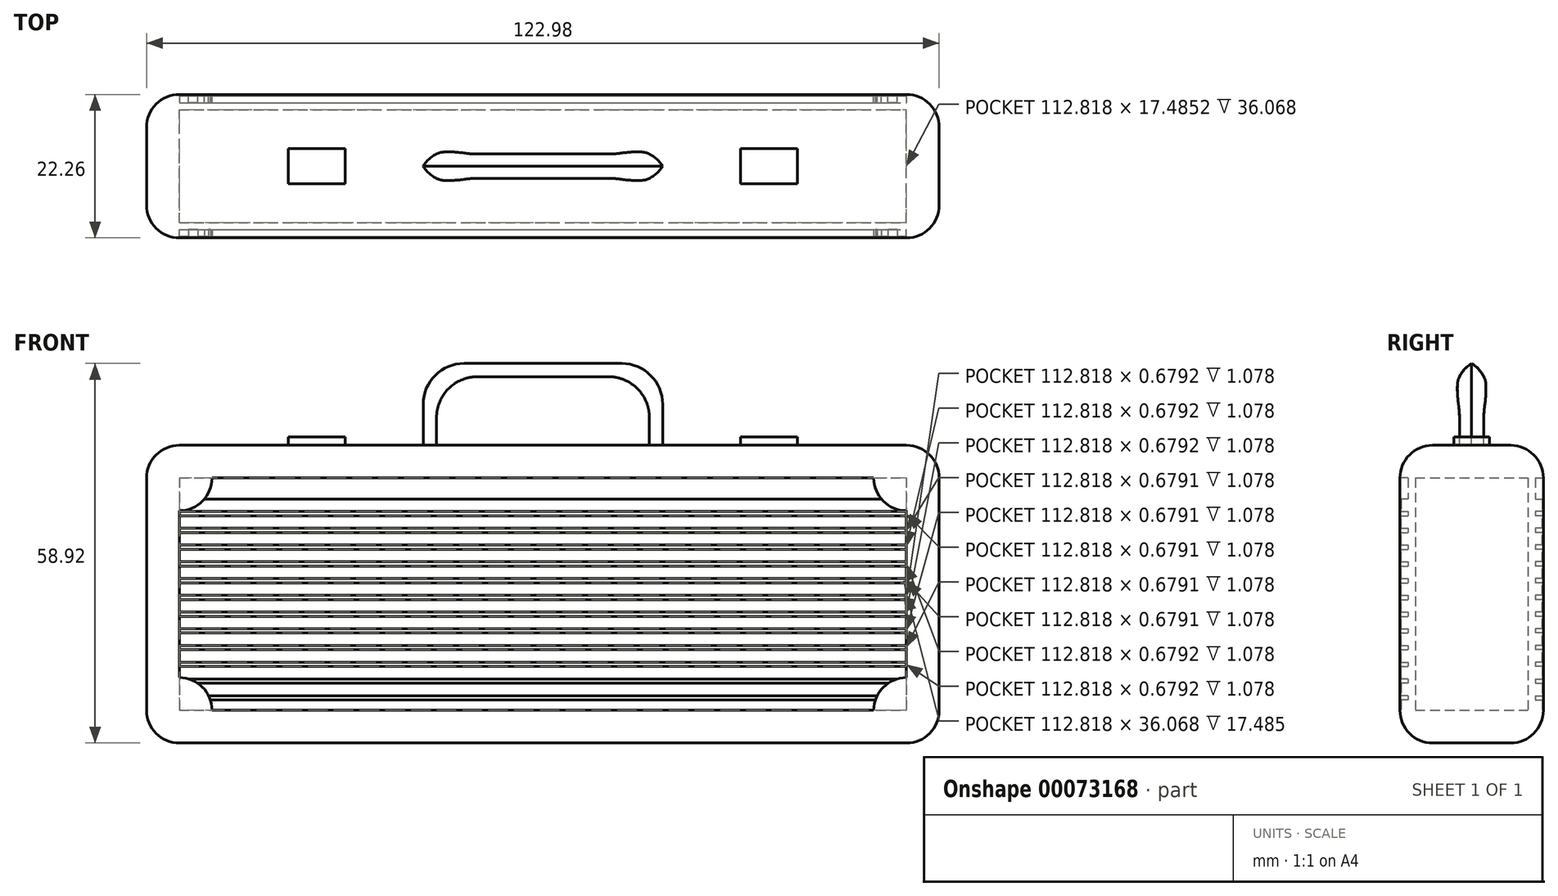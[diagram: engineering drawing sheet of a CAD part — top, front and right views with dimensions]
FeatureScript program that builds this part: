
annotation { "Feature Type Name" : "Feature", "Feature Type Description" : "" }
export const myFeature = defineFeature(function(context is Context, id is Id, definition is map)
    precondition{}
    {
        {
            var Q0;
            Q0=qCreatedBy(makeId("Front.planeOp"),FACE);
            var sketch = newSketch(context, id + "F0", { "sketchPlane" : qUnion([Q0])});
            skLineSegment(sketch, "E0.bottom", {"start": v(61.49, -23.11) * mm, "end": v(-61.49, -23.11) * mm});
            skLineSegment(sketch, "E0.top", {"start": v(61.49, 23.11) * mm, "end": v(-61.49, 23.11) * mm});
            skLineSegment(sketch, "E0.left", {"start": v(61.49, -23.11) * mm, "end": v(61.49, 23.11) * mm});
            skLineSegment(sketch, "E0.right", {"start": v(-61.49, -23.11) * mm, "end": v(-61.49, 23.11) * mm});
            skPoint(sketch, "E0.middle", {"position": v(0, 0) * mm});
            skSolve(sketch);
        }
        {
            var Q0;
            Q0=makeQuery(id+"F0.imprint","IMPRINT",FACE,{"disambiguationData":[TD([[makeQuery(id+"F0.imprint","IMPRINT",EDGE,{"derivedFrom":sQuery(id+"F0.wireOp",EDGE,"E0.bottom")}),-1.0]])]});
            extrude(context, id + "F1", {"entities" : qUnion([Q0]), "depth" : 11.13 * mm});
        }
        {
            var Q0;
            Q0=makeQuery(id+"F1.opExtrude","SWEPT_EDGE",EDGE,{"disambiguationData":[OSD([sQuery(id+"F0.wireOp",EDGE,"E0.top"),sQuery(id+"F0.wireOp",EDGE,"E0.right")])]});
            var Q1;
            Q1=makeQuery(id+"F1.opExtrude","CAP_EDGE",EDGE,{"disambiguationData":[OSD([sQuery(id+"F0.wireOp",EDGE,"E0.right")])],"isStart":false});
            var Q2;
            Q2=makeQuery(id+"F1.opExtrude","CAP_EDGE",EDGE,{"disambiguationData":[OSD([sQuery(id+"F0.wireOp",EDGE,"E0.top")])],"isStart":false});
            var Q3;
            Q3=makeQuery(id+"F1.opExtrude","SWEPT_EDGE",EDGE,{"disambiguationData":[OSD([sQuery(id+"F0.wireOp",EDGE,"E0.bottom"),sQuery(id+"F0.wireOp",EDGE,"E0.right")])]});
            var Q4;
            Q4=makeQuery(id+"F1.opExtrude","CAP_EDGE",EDGE,{"disambiguationData":[OSD([sQuery(id+"F0.wireOp",EDGE,"E0.bottom")])],"isStart":false});
            var Q5;
            Q5=makeQuery(id+"F1.opExtrude","CAP_EDGE",EDGE,{"disambiguationData":[OSD([sQuery(id+"F0.wireOp",EDGE,"E0.left")])],"isStart":false});
            var Q6;
            Q6=makeQuery(id+"F1.opExtrude","SWEPT_EDGE",EDGE,{"disambiguationData":[OSD([sQuery(id+"F0.wireOp",EDGE,"E0.top"),sQuery(id+"F0.wireOp",EDGE,"E0.left")])]});
            var Q7;
            Q7=makeQuery(id+"F1.opExtrude","SWEPT_EDGE",EDGE,{"disambiguationData":[OSD([sQuery(id+"F0.wireOp",EDGE,"E0.bottom"),sQuery(id+"F0.wireOp",EDGE,"E0.left")])]});
            fillet(context, id + "F2", {"entities" : qUnion([Q0, Q1, Q2, Q3, Q4, Q5, Q6, Q7]), "radius" : 5.08 * mm, "tangentPropagation" : true, "allowEdgeOverflow" : false});
        }
        {
            var Q0;
            Q0=qCreatedBy(makeId("Front.planeOp"),FACE);
            var sketch = newSketch(context, id + "F3", { "sketchPlane" : qUnion([Q0])});
            skPoint(sketch, "E1.0", {"position": v(-56.4, 18.03) * mm});
            skPoint(sketch, "E2.0", {"position": v(56.4, -18.03) * mm});
            skLineSegment(sketch, "E3.bottom", {"start": v(-56.4, 18.03) * mm, "end": v(56.4, 18.03) * mm});
            skLineSegment(sketch, "E3.top", {"start": v(-56.4, -18.03) * mm, "end": v(56.4, -18.03) * mm});
            skLineSegment(sketch, "E3.left", {"start": v(-56.4, 18.03) * mm, "end": v(-56.4, -18.03) * mm});
            skLineSegment(sketch, "E3.right", {"start": v(56.4, 18.03) * mm, "end": v(56.4, -18.03) * mm});
            skSolve(sketch);
        }
        {
            var Q0;
            Q0 = qSketchRegion(id + "F3", true);
            extrude(context, id + "F4", {"entities" : qUnion([Q0]), "operationType" : NewBodyOperationType.REMOVE, "depth" : 8.74 * mm});
        }
        {
            var Q0;
            Q0=makeQuery(id+"F1.opExtrude","CAP_FACE",FACE,{"disambiguationData":[OSD([sQuery(id+"F0.wireOp",EDGE,"E0.bottom"),sQuery(id+"F0.wireOp",EDGE,"E0.top"),sQuery(id+"F0.wireOp",EDGE,"E0.left"),sQuery(id+"F0.wireOp",EDGE,"E0.right")])],"isStart":false});
            cPlane(context, id + "F5", {"entities" : qUnion([Q0]), "cplaneType" : CPlaneType.OFFSET, "offset" : 0 * mm, "width" : 152.4 * mm, "height" : 152.4 * mm});
        }
        {
            var Q0;
            Q0=qCreatedBy(id+"F5.planeOp",FACE);
            var sketch = newSketch(context, id + "F6", { "sketchPlane" : qUnion([Q0])});
            skPoint(sketch, "E4.0", {"position": v(-56.4, 18.03) * mm});
            skPoint(sketch, "E5.0", {"position": v(56.4, -18.03) * mm});
            skLineSegment(sketch, "E6.bottom", {"start": v(-56.4, 18.03) * mm, "end": v(56.4, 18.03) * mm});
            skLineSegment(sketch, "E6.top", {"start": v(-56.4, -18.03) * mm, "end": v(56.4, -18.03) * mm});
            skLineSegment(sketch, "E6.left", {"start": v(-56.4, 18.03) * mm, "end": v(-56.4, -18.03) * mm});
            skLineSegment(sketch, "E6.right", {"start": v(56.4, 18.03) * mm, "end": v(56.4, -18.03) * mm});
            skSolve(sketch);
        }
        {
            var Q0;
            Q0 = qSketchRegion(id + "F6", true);
            extrude(context, id + "F7", {"entities" : qUnion([Q0]), "operationType" : NewBodyOperationType.REMOVE, "oppositeDirection" : true, "depth" : 1.27 * mm});
        }
        {
            var Q0;
            Q0=qCreatedBy(id+"F5.planeOp",FACE);
            var sketch = newSketch(context, id + "F8", { "sketchPlane" : qUnion([Q0])});
            skLineSegment(sketch, "E7.0", {"start": v(-56.4, 18.03) * mm, "end": v(-56.4, -18.03) * mm});
            skLineSegment(sketch, "E8.0", {"start": v(56.4, 18.03) * mm, "end": v(-56.4, 18.03) * mm});
            skLineSegment(sketch, "E9", {"start": v(-56.4, 18.03) * mm, "end": v(-50.64, 18.03) * mm});
            skLineSegment(sketch, "E10", {"start": v(-56.4, 18.03) * mm, "end": v(-56.4, 14.08) * mm});
            skSolve(sketch);
        }
        {
            var Q0;
            Q0=makeQuery(id+"F1.opExtrude","SWEPT_FACE",FACE,{"disambiguationData":[OSD([sQuery(id+"F0.wireOp",EDGE,"E0.top")])]});
            cPlane(context, id + "F9", {"entities" : qUnion([Q0]), "cplaneType" : CPlaneType.OFFSET, "offset" : 0 * mm, "width" : 152.4 * mm, "height" : 152.4 * mm});
        }
        {
            var Q0;
            Q0=makeQuery(id+"F1.opExtrude","CAP_FACE",FACE,{"disambiguationData":[OSD([sQuery(id+"F0.wireOp",EDGE,"E0.bottom"),sQuery(id+"F0.wireOp",EDGE,"E0.top"),sQuery(id+"F0.wireOp",EDGE,"E0.left"),sQuery(id+"F0.wireOp",EDGE,"E0.right")])],"isStart":true});
            cPlane(context, id + "F10", {"entities" : qUnion([Q0]), "cplaneType" : CPlaneType.OFFSET, "offset" : 0 * mm, "width" : 152.4 * mm, "height" : 152.4 * mm});
        }
        {
            var Q0;
            Q0=qCreatedBy(id+"F10.planeOp",FACE);
            var sketch = newSketch(context, id + "F11", { "sketchPlane" : qUnion([Q0])});
            skLineSegment(sketch, "E11.0", {"start": v(-56.4, 23.11) * mm, "end": v(56.4, 23.11) * mm});
            skLineSegment(sketch, "E12.bottom", {"start": v(-18.58, 23.11) * mm, "end": v(18.58, 23.11) * mm});
            skLineSegment(sketch, "E12.top", {"start": v(-12.23, 35.81) * mm, "end": v(12.23, 35.81) * mm});
            skLineSegment(sketch, "E12.left", {"start": v(-18.58, 23.11) * mm, "end": v(-18.58, 29.46) * mm});
            skLineSegment(sketch, "E12.right", {"start": v(18.58, 23.11) * mm, "end": v(18.58, 29.46) * mm});
            skPoint(sketch, "E12.middle", {"position": v(0, 29.46) * mm});
            skPoint(sketch, "E13.visualSharp", {"position": v(18.58, 35.81) * mm});
            skArc(sketch, "E13.filletArc", {"start": v(18.58, 29.46) * mm, "mid": v(16.72, 33.95) * mm, "end": v(12.23, 35.81) * mm});
            skPoint(sketch, "E14.visualSharp", {"position": v(-18.58, 35.81) * mm});
            skArc(sketch, "E14.filletArc", {"start": v(-12.23, 35.81) * mm, "mid": v(-16.72, 33.95) * mm, "end": v(-18.58, 29.46) * mm});
            skLineSegment(sketch, "E15.top", {"start": v(-10.17, 33.76) * mm, "end": v(10.15, 33.76) * mm});
            skLineSegment(sketch, "E15.left", {"start": v(-16.52, 23.11) * mm, "end": v(-16.52, 27.41) * mm});
            skLineSegment(sketch, "E15.right", {"start": v(16.5, 23.11) * mm, "end": v(16.5, 27.41) * mm});
            skArc(sketch, "E16.filletArc", {"start": v(16.5, 27.41) * mm, "mid": v(14.64, 31.9) * mm, "end": v(10.15, 33.76) * mm});
            skArc(sketch, "E17.filletArc", {"start": v(-10.17, 33.76) * mm, "mid": v(-14.66, 31.9) * mm, "end": v(-16.52, 27.41) * mm});
            skSolve(sketch);
        }
        {
            var Q0;
            Q0=makeQuery(id+"F11.imprint","IMPRINT",FACE,{"disambiguationData":[TD([[makeQuery(id+"F11.imprint","IMPRINT",EDGE,{"derivedFrom":sQuery(id+"F11.wireOp",EDGE,"E12.top")}),-1.0]])]});
            extrude(context, id + "F12", {"entities" : qUnion([Q0]), "operationType" : NewBodyOperationType.ADD, "oppositeDirection" : true, "depth" : 2.42 * mm});
        }
        {
            var Q0;
            Q0=makeQuery(id+"F12.opExtrude","CAP_EDGE",EDGE,{"disambiguationData":[OSD([sQuery(id+"F11.wireOp",EDGE,"E13.filletArc")])],"isStart":false});
            fillet(context, id + "F13", {"entities" : qUnion([Q0]), "radius" : 5.08 * mm, "tangentPropagation" : true, "allowEdgeOverflow" : false});
        }
        {
            var Q0;
            Q0=makeQuery(id+"F7.boolean.opBoolean","COPY",FACE,{"derivedFrom":makeQuery(id+"F7.opExtrude","CAP_FACE",FACE,{"disambiguationData":[OSD([sQuery(id+"F6.wireOp",EDGE,"E6.bottom"),sQuery(id+"F6.wireOp",EDGE,"E6.top"),sQuery(id+"F6.wireOp",EDGE,"E6.left"),sQuery(id+"F6.wireOp",EDGE,"E6.right")])],"isStart":false})});
            cPlane(context, id + "F14", {"entities" : qUnion([Q0]), "cplaneType" : CPlaneType.OFFSET, "offset" : 0 * mm, "width" : 152.4 * mm, "height" : 152.4 * mm});
        }
        {
            var Q0;
            Q0=qCreatedBy(id+"F14.planeOp",FACE);
            var sketch = newSketch(context, id + "F15", { "sketchPlane" : qUnion([Q0])});
            skLineSegment(sketch, "E18.0.0", {"start": v(56.4, 18.03) * mm, "end": v(-56.4, 18.03) * mm});
            skLineSegment(sketch, "E18.0.1", {"start": v(-56.4, 18.03) * mm, "end": v(-56.4, -18.03) * mm});
            skLineSegment(sketch, "E18.0.2", {"start": v(-56.4, -18.03) * mm, "end": v(56.4, -18.03) * mm});
            skLineSegment(sketch, "E18.0.3", {"start": v(56.4, -18.03) * mm, "end": v(56.4, 18.03) * mm});
            skLineSegment(sketch, "E19.bottom", {"start": v(-56.4, 18.03) * mm, "end": v(56.4, 18.03) * mm});
            skLineSegment(sketch, "E19.top", {"start": v(-56.4, 14.76) * mm, "end": v(56.4, 14.76) * mm});
            skLineSegment(sketch, "E19.left", {"start": v(-56.4, 18.03) * mm, "end": v(-56.4, 14.76) * mm});
            skLineSegment(sketch, "E19.right", {"start": v(56.4, 18.03) * mm, "end": v(56.4, 14.76) * mm});
            skLineSegment(sketch, "E20.1.0.0", {"start": v(-56.4, 15.43) * mm, "end": v(56.4, 15.43) * mm});
            skLineSegment(sketch, "E20.1.0.1", {"start": v(-56.4, 12.16) * mm, "end": v(56.4, 12.16) * mm});
            skLineSegment(sketch, "E20.1.0.2", {"start": v(56.4, 15.43) * mm, "end": v(-56.4, 15.43) * mm});
            skLineSegment(sketch, "E20.1.0.3", {"start": v(56.4, 15.43) * mm, "end": v(56.4, 12.16) * mm});
            skLineSegment(sketch, "E20.2.0.0", {"start": v(-56.4, 12.83) * mm, "end": v(56.4, 12.83) * mm});
            skLineSegment(sketch, "E20.2.0.1", {"start": v(-56.4, 9.56) * mm, "end": v(56.4, 9.56) * mm});
            skLineSegment(sketch, "E20.2.0.2", {"start": v(56.4, 12.83) * mm, "end": v(-56.4, 12.83) * mm});
            skLineSegment(sketch, "E20.2.0.3", {"start": v(56.4, 12.83) * mm, "end": v(56.4, 9.56) * mm});
            skLineSegment(sketch, "E20.3.0.0", {"start": v(-56.4, 10.24) * mm, "end": v(56.4, 10.24) * mm});
            skLineSegment(sketch, "E20.3.0.1", {"start": v(-56.4, 6.96) * mm, "end": v(56.4, 6.96) * mm});
            skLineSegment(sketch, "E20.3.0.2", {"start": v(56.4, 10.24) * mm, "end": v(-56.4, 10.24) * mm});
            skLineSegment(sketch, "E20.3.0.3", {"start": v(56.4, 10.24) * mm, "end": v(56.4, 6.96) * mm});
            skLineSegment(sketch, "E20.4.0.0", {"start": v(-56.4, 7.64) * mm, "end": v(56.4, 7.64) * mm});
            skLineSegment(sketch, "E20.4.0.1", {"start": v(-56.4, 4.36) * mm, "end": v(56.4, 4.36) * mm});
            skLineSegment(sketch, "E20.4.0.2", {"start": v(56.4, 7.64) * mm, "end": v(-56.4, 7.64) * mm});
            skLineSegment(sketch, "E20.4.0.3", {"start": v(56.4, 7.64) * mm, "end": v(56.4, 4.36) * mm});
            skLineSegment(sketch, "E20.5.0.0", {"start": v(-56.4, 5.04) * mm, "end": v(56.4, 5.04) * mm});
            skLineSegment(sketch, "E20.5.0.1", {"start": v(-56.4, 1.76) * mm, "end": v(56.4, 1.76) * mm});
            skLineSegment(sketch, "E20.5.0.2", {"start": v(56.4, 5.04) * mm, "end": v(-56.4, 5.04) * mm});
            skLineSegment(sketch, "E20.5.0.3", {"start": v(56.4, 5.04) * mm, "end": v(56.4, 1.76) * mm});
            skLineSegment(sketch, "E20.6.0.0", {"start": v(-56.4, 2.44) * mm, "end": v(56.4, 2.44) * mm});
            skLineSegment(sketch, "E20.6.0.1", {"start": v(-56.4, -0.84) * mm, "end": v(56.4, -0.84) * mm});
            skLineSegment(sketch, "E20.6.0.2", {"start": v(56.4, 2.44) * mm, "end": v(-56.4, 2.44) * mm});
            skLineSegment(sketch, "E20.6.0.3", {"start": v(56.4, 2.44) * mm, "end": v(56.4, -0.84) * mm});
            skLineSegment(sketch, "E20.7.0.0", {"start": v(-56.4, -0.16) * mm, "end": v(56.4, -0.16) * mm});
            skLineSegment(sketch, "E20.7.0.1", {"start": v(-56.4, -3.44) * mm, "end": v(56.4, -3.44) * mm});
            skLineSegment(sketch, "E20.7.0.2", {"start": v(56.4, -0.16) * mm, "end": v(-56.4, -0.16) * mm});
            skLineSegment(sketch, "E20.7.0.3", {"start": v(56.4, -0.16) * mm, "end": v(56.4, -3.44) * mm});
            skLineSegment(sketch, "E20.8.0.0", {"start": v(-56.4, -2.76) * mm, "end": v(56.4, -2.76) * mm});
            skLineSegment(sketch, "E20.8.0.1", {"start": v(-56.4, -6.04) * mm, "end": v(56.4, -6.04) * mm});
            skLineSegment(sketch, "E20.8.0.2", {"start": v(56.4, -2.76) * mm, "end": v(-56.4, -2.76) * mm});
            skLineSegment(sketch, "E20.8.0.3", {"start": v(56.4, -2.76) * mm, "end": v(56.4, -6.04) * mm});
            skLineSegment(sketch, "E20.9.0.0", {"start": v(-56.4, -5.36) * mm, "end": v(56.4, -5.36) * mm});
            skLineSegment(sketch, "E20.9.0.1", {"start": v(-56.4, -8.64) * mm, "end": v(56.4, -8.64) * mm});
            skLineSegment(sketch, "E20.9.0.2", {"start": v(56.4, -5.36) * mm, "end": v(-56.4, -5.36) * mm});
            skLineSegment(sketch, "E20.9.0.3", {"start": v(56.4, -5.36) * mm, "end": v(56.4, -8.64) * mm});
            skLineSegment(sketch, "E20.10.0.0", {"start": v(-56.4, -7.96) * mm, "end": v(56.4, -7.96) * mm});
            skLineSegment(sketch, "E20.10.0.1", {"start": v(-56.4, -11.24) * mm, "end": v(56.4, -11.24) * mm});
            skLineSegment(sketch, "E20.10.0.2", {"start": v(56.4, -7.96) * mm, "end": v(-56.4, -7.96) * mm});
            skLineSegment(sketch, "E20.10.0.3", {"start": v(56.4, -7.96) * mm, "end": v(56.4, -11.24) * mm});
            skLineSegment(sketch, "E20.11.0.0", {"start": v(-56.4, -10.56) * mm, "end": v(56.4, -10.56) * mm});
            skLineSegment(sketch, "E20.11.0.1", {"start": v(-56.4, -13.84) * mm, "end": v(56.4, -13.84) * mm});
            skLineSegment(sketch, "E20.11.0.2", {"start": v(56.4, -10.56) * mm, "end": v(-56.4, -10.56) * mm});
            skLineSegment(sketch, "E20.11.0.3", {"start": v(56.4, -10.56) * mm, "end": v(56.4, -13.84) * mm});
            skLineSegment(sketch, "E20.12.0.0", {"start": v(-56.4, -13.16) * mm, "end": v(56.4, -13.16) * mm});
            skLineSegment(sketch, "E20.12.0.1", {"start": v(-56.4, -16.44) * mm, "end": v(56.4, -16.44) * mm});
            skLineSegment(sketch, "E20.12.0.2", {"start": v(56.4, -13.16) * mm, "end": v(-56.4, -13.16) * mm});
            skLineSegment(sketch, "E20.12.0.3", {"start": v(56.4, -13.16) * mm, "end": v(56.4, -16.44) * mm});
            skLineSegment(sketch, "E20.13.0.0", {"start": v(-56.4, -15.76) * mm, "end": v(56.4, -15.76) * mm});
            skLineSegment(sketch, "E20.13.0.1", {"start": v(-56.4, -19.04) * mm, "end": v(56.4, -19.04) * mm});
            skLineSegment(sketch, "E20.13.0.2", {"start": v(56.4, -15.76) * mm, "end": v(-56.4, -15.76) * mm});
            skLineSegment(sketch, "E20.13.0.3", {"start": v(56.4, -15.76) * mm, "end": v(56.4, -19.04) * mm});
            skLineSegment(sketch, "E20.direction1", {"start": v(-56.4, 14.76) * mm, "end": v(-56.4, 12.16) * mm, "construction": true});
            skSolve(sketch);
        }
        {
            var Q0;
            Q0=qCreatedBy(id+"F9.planeOp",FACE);
            var sketch = newSketch(context, id + "F16", { "sketchPlane" : qUnion([Q0])});
            skLineSegment(sketch, "E21.0", {"start": v(56.4, 0) * mm, "end": v(18.58, 0) * mm});
            skLineSegment(sketch, "E22.0", {"start": v(-18.58, 0) * mm, "end": v(-56.4, 0) * mm});
            skLineSegment(sketch, "E23.bottom", {"start": v(30.69, 0) * mm, "end": v(39.5, 0) * mm});
            skLineSegment(sketch, "E23.top", {"start": v(30.69, -2.76) * mm, "end": v(39.5, -2.76) * mm});
            skLineSegment(sketch, "E23.left", {"start": v(30.69, 0) * mm, "end": v(30.69, -2.76) * mm});
            skLineSegment(sketch, "E23.right", {"start": v(39.5, 0) * mm, "end": v(39.5, -2.76) * mm});
            skLineSegment(sketch, "E24.MirrorCS", {"start": v(-30.69, 0) * mm, "end": v(-30.69, -2.76) * mm});
            skLineSegment(sketch, "E25.MirrorCS", {"start": v(-30.69, 0) * mm, "end": v(-39.5, 0) * mm});
            skLineSegment(sketch, "E26.MirrorCS", {"start": v(-39.5, 0) * mm, "end": v(-39.5, -2.76) * mm});
            skLineSegment(sketch, "E27.MirrorCS", {"start": v(-30.69, -2.76) * mm, "end": v(-39.5, -2.76) * mm});
            skSolve(sketch);
        }
        {
            var Q0;
            Q0 = qSketchRegion(id + "F16", true);
            extrude(context, id + "F17", {"entities" : qUnion([Q0]), "operationType" : NewBodyOperationType.ADD, "depth" : 1.27 * mm});
        }
        {
            var Q0;
            Q0=qCreatedBy(id+"F5.planeOp",FACE);
            var sketch = newSketch(context, id + "F18", { "sketchPlane" : qUnion([Q0])});
            skPoint(sketch, "E28.0", {"position": v(-56.4, 18.03) * mm});
            skLineSegment(sketch, "E29.0", {"start": v(-56.4, 18.03) * mm, "end": v(-50.64, 18.03) * mm});
            skLineSegment(sketch, "E30.0", {"start": v(-56.4, 18.03) * mm, "end": v(-56.4, 14.08) * mm});
            skLineSegment(sketch, "E31.0", {"start": v(-56.4, 13.38) * mm, "end": v(-56.4, 12.84) * mm});
            skLineSegment(sketch, "E31.1", {"start": v(-56.4, 10.78) * mm, "end": v(-56.4, 10.24) * mm});
            skLineSegment(sketch, "E31.2", {"start": v(-56.4, 2.99) * mm, "end": v(-56.4, 2.44) * mm});
            skLineSegment(sketch, "E31.3", {"start": v(-56.4, 8.18) * mm, "end": v(-56.4, 7.64) * mm});
            skLineSegment(sketch, "E31.4", {"start": v(-56.4, 5.58) * mm, "end": v(-56.4, 5.04) * mm});
            skLineSegment(sketch, "E31.5", {"start": v(-56.4, 12.84) * mm, "end": v(-56.4, 10.78) * mm});
            skLineSegment(sketch, "E31.6", {"start": v(-56.4, 10.24) * mm, "end": v(-56.4, 8.18) * mm});
            skLineSegment(sketch, "E31.7", {"start": v(-56.4, 7.64) * mm, "end": v(-56.4, 5.58) * mm});
            skLineSegment(sketch, "E31.8", {"start": v(-56.4, 5.04) * mm, "end": v(-56.4, 2.99) * mm});
            skArc(sketch, "E32", {"start": v(-51.33, 18.03) * mm, "mid": v(-52.82, 14.44) * mm, "end": v(-56.4, 12.95) * mm});
            skArc(sketch, "E33.MirrorCS", {"start": v(-51.33, -18.03) * mm, "mid": v(-52.82, -14.44) * mm, "end": v(-56.4, -12.95) * mm});
            skArc(sketch, "E34.MirrorCS", {"start": v(51.33, 18.03) * mm, "mid": v(52.82, 14.44) * mm, "end": v(56.4, 12.95) * mm});
            skArc(sketch, "E35.MirrorCS", {"start": v(51.33, -18.03) * mm, "mid": v(52.82, -14.44) * mm, "end": v(56.4, -12.95) * mm});
            skLineSegment(sketch, "E36", {"start": v(-51.33, 18.03) * mm, "end": v(-56.4, 18.03) * mm});
            skLineSegment(sketch, "E37", {"start": v(-56.4, 18.03) * mm, "end": v(-56.4, 12.95) * mm});
            skLineSegment(sketch, "E38", {"start": v(-56.4, -12.95) * mm, "end": v(-56.4, -18.03) * mm});
            skLineSegment(sketch, "E39", {"start": v(-51.33, -18.03) * mm, "end": v(-56.4, -18.03) * mm});
            skLineSegment(sketch, "E40", {"start": v(51.33, -18.03) * mm, "end": v(56.4, -18.03) * mm});
            skLineSegment(sketch, "E41", {"start": v(56.4, -12.95) * mm, "end": v(56.4, -18.03) * mm});
            skLineSegment(sketch, "E42", {"start": v(56.4, 18.03) * mm, "end": v(56.4, 12.95) * mm});
            skLineSegment(sketch, "E43", {"start": v(56.4, 18.03) * mm, "end": v(51.33, 18.03) * mm});
            skSolve(sketch);
        }
        {
            var Q0;
            {var subQ0=sQuery(id+"F15.wireOp",EDGE,"E19.bottom");Q0=makeQuery(id+"F15.imprint","IMPRINT",FACE,{"disambiguationData":[TD([[makeQuery(id+"F15.imprint","IMPRINT",EDGE,{"derivedFrom":subQ0}),-1.0]])]});}
            var Q1;
            {var subQ0=sQuery(id+"F15.wireOp",EDGE,"E19.top");Q1=makeQuery(id+"F15.imprint","IMPRINT",FACE,{"disambiguationData":[TD([[makeQuery(id+"F15.imprint","IMPRINT",EDGE,{"derivedFrom":subQ0}),-1.0]])]});}
            var Q2;
            {var subQ0=sQuery(id+"F15.wireOp",EDGE,"E20.1.0.1");Q2=makeQuery(id+"F15.imprint","IMPRINT",FACE,{"disambiguationData":[TD([[makeQuery(id+"F15.imprint","IMPRINT",EDGE,{"derivedFrom":subQ0}),-1.0]])]});}
            var Q3;
            {var subQ0=sQuery(id+"F15.wireOp",EDGE,"E20.2.0.1");Q3=makeQuery(id+"F15.imprint","IMPRINT",FACE,{"disambiguationData":[TD([[makeQuery(id+"F15.imprint","IMPRINT",EDGE,{"derivedFrom":subQ0}),-1.0]])]});}
            var Q4;
            {var subQ0=sQuery(id+"F15.wireOp",EDGE,"E20.3.0.1");Q4=makeQuery(id+"F15.imprint","IMPRINT",FACE,{"disambiguationData":[TD([[makeQuery(id+"F15.imprint","IMPRINT",EDGE,{"derivedFrom":subQ0}),-1.0]])]});}
            var Q5;
            {var subQ0=sQuery(id+"F15.wireOp",EDGE,"E20.4.0.1");Q5=makeQuery(id+"F15.imprint","IMPRINT",FACE,{"disambiguationData":[TD([[makeQuery(id+"F15.imprint","IMPRINT",EDGE,{"derivedFrom":subQ0}),-1.0]])]});}
            var Q6;
            {var subQ0=sQuery(id+"F15.wireOp",EDGE,"E20.5.0.1");Q6=makeQuery(id+"F15.imprint","IMPRINT",FACE,{"disambiguationData":[TD([[makeQuery(id+"F15.imprint","IMPRINT",EDGE,{"derivedFrom":subQ0}),-1.0]])]});}
            var Q7;
            {var subQ0=sQuery(id+"F15.wireOp",EDGE,"E20.6.0.1");Q7=makeQuery(id+"F15.imprint","IMPRINT",FACE,{"disambiguationData":[TD([[makeQuery(id+"F15.imprint","IMPRINT",EDGE,{"derivedFrom":subQ0}),-1.0]])]});}
            var Q8;
            {var subQ0=sQuery(id+"F15.wireOp",EDGE,"E20.7.0.1");Q8=makeQuery(id+"F15.imprint","IMPRINT",FACE,{"disambiguationData":[TD([[makeQuery(id+"F15.imprint","IMPRINT",EDGE,{"derivedFrom":subQ0}),-1.0]])]});}
            var Q9;
            {var subQ0=sQuery(id+"F15.wireOp",EDGE,"E20.8.0.1");Q9=makeQuery(id+"F15.imprint","IMPRINT",FACE,{"disambiguationData":[TD([[makeQuery(id+"F15.imprint","IMPRINT",EDGE,{"derivedFrom":subQ0}),-1.0]])]});}
            var Q10;
            {var subQ0=sQuery(id+"F15.wireOp",EDGE,"E20.9.0.1");Q10=makeQuery(id+"F15.imprint","IMPRINT",FACE,{"disambiguationData":[TD([[makeQuery(id+"F15.imprint","IMPRINT",EDGE,{"derivedFrom":subQ0}),-1.0]])]});}
            var Q11;
            {var subQ0=sQuery(id+"F15.wireOp",EDGE,"E20.10.0.1");Q11=makeQuery(id+"F15.imprint","IMPRINT",FACE,{"disambiguationData":[TD([[makeQuery(id+"F15.imprint","IMPRINT",EDGE,{"derivedFrom":subQ0}),-1.0]])]});}
            var Q12;
            {var subQ0=sQuery(id+"F15.wireOp",EDGE,"E20.11.0.1");Q12=makeQuery(id+"F15.imprint","IMPRINT",FACE,{"disambiguationData":[TD([[makeQuery(id+"F15.imprint","IMPRINT",EDGE,{"derivedFrom":subQ0}),-1.0]])]});}
            var Q13;
            {var subQ0=sQuery(id+"F15.wireOp",EDGE,"E18.0.2");Q13=makeQuery(id+"F15.imprint","IMPRINT",FACE,{"disambiguationData":[TD([[makeQuery(id+"F15.imprint","IMPRINT",EDGE,{"derivedFrom":subQ0}),1.0]])]});}
            extrude(context, id + "F19", {"entities" : qUnion([Q0, Q1, Q2, Q3, Q4, Q5, Q6, Q7, Q8, Q9, Q10, Q11, Q12, Q13]), "operationType" : NewBodyOperationType.ADD, "depth" : 1.08 * mm});
        }
        {
            var Q0;
            Q0 = qSketchRegion(id + "F18", true);
            extrude(context, id + "F20", {"entities" : qUnion([Q0]), "operationType" : NewBodyOperationType.ADD, "oppositeDirection" : true, "depth" : 2.2 * mm});
        }
        {
            var Q0;
            Q0=makeQuery(id+"F1.opExtrude","SWEPT_BODY",BODY,{"disambiguationData":[OSD([sQuery(id+"F0.wireOp",EDGE,"E0.bottom"),sQuery(id+"F0.wireOp",EDGE,"E0.top"),sQuery(id+"F0.wireOp",EDGE,"E0.left"),sQuery(id+"F0.wireOp",EDGE,"E0.right")])]});
            var Q1;
            Q1=qCreatedBy(makeId("Front.planeOp"),FACE);
            mirror(context, id + "F21", {"operationType" : NewBodyOperationType.ADD, "entities" : qUnion([Q0]), "mirrorPlane" : qUnion([Q1])});
        }
    });
